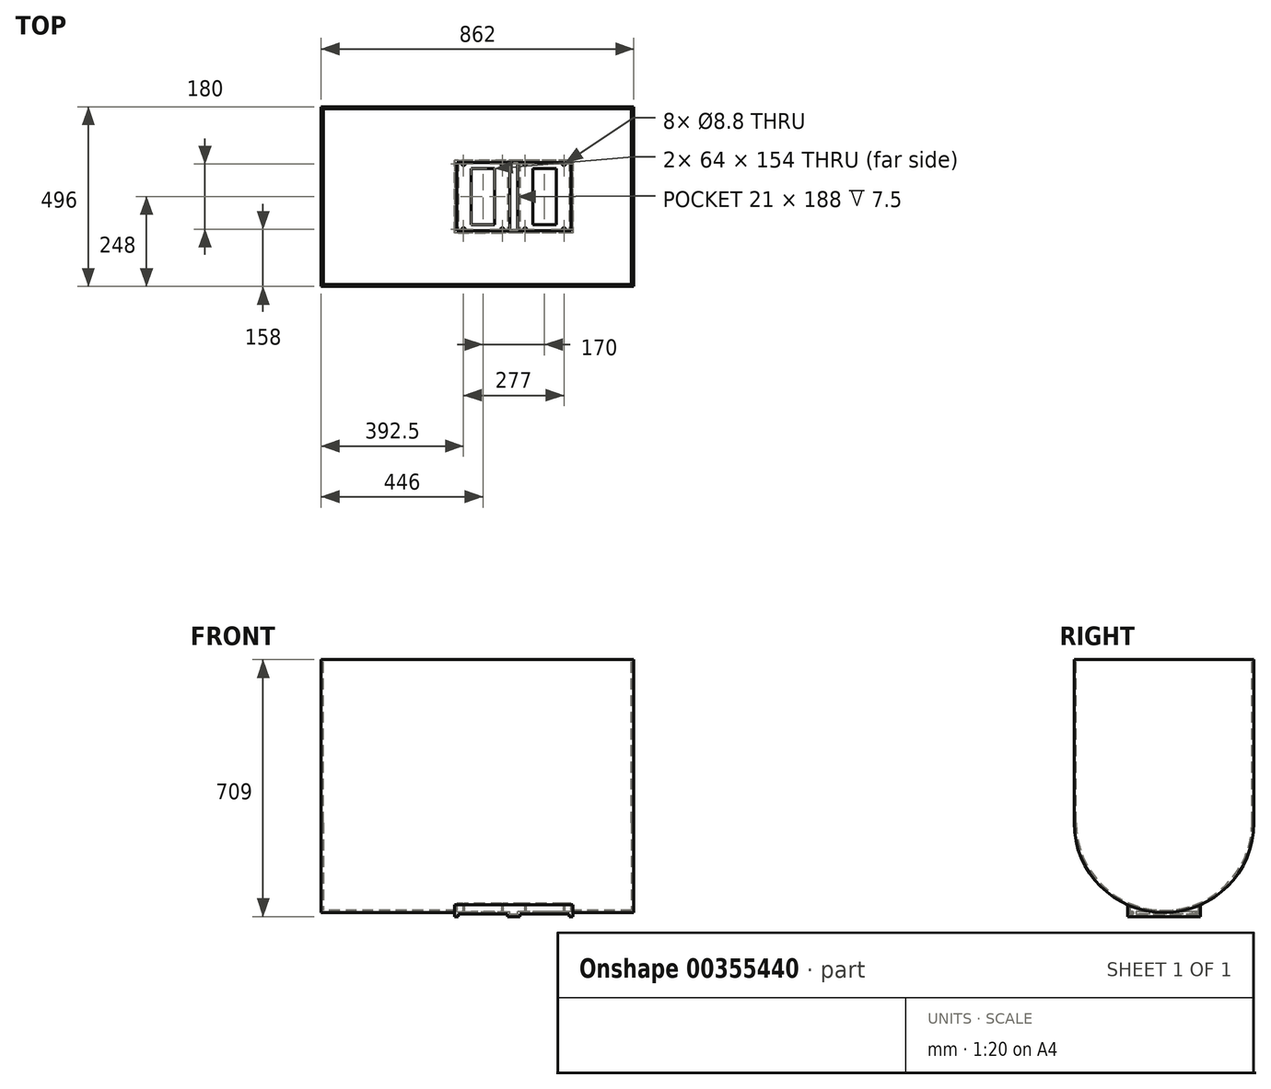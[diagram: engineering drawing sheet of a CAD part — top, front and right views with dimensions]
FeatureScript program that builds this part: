
annotation { "Feature Type Name" : "Feature", "Feature Type Description" : "" }
export const myFeature = defineFeature(function(context is Context, id is Id, definition is map)
    precondition{}
    {
        {
            var Q0;
            Q0=qCreatedBy(makeId("Right.planeOp"),FACE);
            var sketch = newSketch(context, id + "F0", { "sketchPlane" : qUnion([Q0])});
            skArc(sketch, "E0", {"start": v(-248, 0) * mm, "mid": v(0, -248) * mm, "end": v(248, 0) * mm});
            skLineSegment(sketch, "E1", {"start": v(0, -259) * mm, "end": v(0, 710.2) * mm, "construction": true});
            skLineSegment(sketch, "E2.0", {"start": v(248, 0) * mm, "end": v(248, 450) * mm});
            skLineSegment(sketch, "E3.MirrorCS", {"start": v(-248, 0) * mm, "end": v(-248, 450) * mm});
            skLineSegment(sketch, "E4", {"start": v(-248, 0) * mm, "end": v(248, 0) * mm, "construction": true});
            skLineSegment(sketch, "E5.MirrorCS", {"start": v(-248, 450) * mm, "end": v(248, 450) * mm});
            skPoint(sketch, "E6.orphan", {"position": v(-248, 710.2) * mm});
            skPoint(sketch, "E7.orphan", {"position": v(248, 710.2) * mm});
            skLineSegment(sketch, "E8.bottom", {"start": v(100, -259) * mm, "end": v(-100, -259) * mm});
            skLineSegment(sketch, "E8.left", {"start": v(100, -259) * mm, "end": v(100, -226.94) * mm});
            skLineSegment(sketch, "E8.right", {"start": v(-100, -259) * mm, "end": v(-100, -226.94) * mm});
            skPoint(sketch, "E8.middle", {"position": v(0, -248) * mm});
            skPoint(sketch, "E9.orphan", {"position": v(-100, -237) * mm});
            skPoint(sketch, "E10.orphan", {"position": v(100, -237) * mm});
            skSolve(sketch);
        }
        {
            var Q0;
            {var subQ0=sQuery(id+"F0.wireOp",EDGE,"E2.0");Q0=makeQuery(id+"F0.imprint","IMPRINT",FACE,{"disambiguationData":[TD([[makeQuery(id+"F0.imprint","IMPRINT",EDGE,{"derivedFrom":subQ0}),1.0]])]});}
            extrude(context, id + "F1", {"entities" : qUnion([Q0]), "endBound" : BoundingType.SYMMETRIC, "depth" : 862 * mm});
        }
        {
            var Q0;
            Q0=makeQuery(id+"F0.imprint","IMPRINT",FACE,{"disambiguationData":[TD([[makeQuery(id+"F0.imprint","IMPRINT",EDGE,{"derivedFrom":sQuery(id+"F0.wireOp",EDGE,"E8.bottom")}),-1.0]])]});
            extrude(context, id + "F2", {"entities" : qUnion([Q0]), "operationType" : NewBodyOperationType.ADD, "depth" : 263.5 * mm, "hasSecondDirection" : true, "secondDirectionOppositeDirection" : true, "secondDirectionDepth" : 63.5 * mm});
        }
        {
            var Q0;
            Q0=makeQuery(id+"F2.opExtrude","SWEPT_FACE",FACE,{"disambiguationData":[OSD([sQuery(id+"F0.wireOp",EDGE,"E8.right")])]});
            var sketch = newSketch(context, id + "F3", { "sketchPlane" : qUnion([Q0])});
            skLineSegment(sketch, "E11.bottom", {"start": v(-53.5, -269) * mm, "end": v(83.5, -269) * mm});
            skLineSegment(sketch, "E11.top", {"start": v(-53.5, -251.5) * mm, "end": v(83.5, -251.5) * mm});
            skLineSegment(sketch, "E11.left", {"start": v(-53.5, -269) * mm, "end": v(-53.5, -251.5) * mm});
            skLineSegment(sketch, "E11.right", {"start": v(83.5, -269) * mm, "end": v(83.5, -251.5) * mm});
            skLineSegment(sketch, "E12", {"start": v(100, -259) * mm, "end": v(100, -189.41) * mm, "construction": true});
            skLineSegment(sketch, "E13.MirrorCS", {"start": v(253.5, -269) * mm, "end": v(116.5, -269) * mm});
            skLineSegment(sketch, "E14.MirrorCS", {"start": v(253.5, -251.5) * mm, "end": v(116.5, -251.5) * mm});
            skLineSegment(sketch, "E15.MirrorCS", {"start": v(116.5, -269) * mm, "end": v(116.5, -251.5) * mm});
            skLineSegment(sketch, "E16.MirrorCS", {"start": v(253.5, -269) * mm, "end": v(253.5, -251.5) * mm});
            skSolve(sketch);
        }
        {
            var Q0;
            Q0 = qSketchRegion(id + "F3", true);
            extrude(context, id + "F4", {"entities" : qUnion([Q0]), "operationType" : NewBodyOperationType.REMOVE, "oppositeDirection" : true, "depth" : 250 * mm});
        }
        {
            var Q0;
            Q0=makeQuery(id+"F1.opExtrude","SWEPT_FACE",FACE,{"disambiguationData":[OSD([sQuery(id+"F0.wireOp",EDGE,"E5.MirrorCS")])]});
            shell(context, id + "F5", {"entities" : qUnion([Q0]), "thickness" : 6 * mm});
        }
        {
            var Q0;
            Q0=makeQuery(id+"F4.boolean.opBoolean","COPY",FACE,{"derivedFrom":makeQuery(id+"F4.opExtrude","SWEPT_FACE",FACE,{"disambiguationData":[OSD([sQuery(id+"F3.wireOp",EDGE,"E14.MirrorCS")])]})});
            var sketch = newSketch(context, id + "F6", { "sketchPlane" : qUnion([Q0])});
            skLineSegment(sketch, "E17.bottom", {"start": v(153, 77) * mm, "end": v(217, 77) * mm});
            skLineSegment(sketch, "E17.top", {"start": v(153, -77) * mm, "end": v(217, -77) * mm});
            skLineSegment(sketch, "E17.left", {"start": v(153, 77) * mm, "end": v(153, -77) * mm});
            skLineSegment(sketch, "E17.right", {"start": v(217, 77) * mm, "end": v(217, -77) * mm});
            skLineSegment(sketch, "E18", {"start": v(100, 100) * mm, "end": v(100, -121.49) * mm, "construction": true});
            skLineSegment(sketch, "E19.MirrorCS", {"start": v(-17, 77) * mm, "end": v(-17, -77) * mm});
            skLineSegment(sketch, "E20.MirrorCS", {"start": v(47, 77) * mm, "end": v(47, -77) * mm});
            skLineSegment(sketch, "E21.MirrorCS", {"start": v(47, -77) * mm, "end": v(-17, -77) * mm});
            skLineSegment(sketch, "E22.MirrorCS", {"start": v(47, 77) * mm, "end": v(-17, 77) * mm});
            skSolve(sketch);
        }
        {
            var Q0;
            Q0=makeQuery(id+"F6.imprint","IMPRINT",FACE,{"disambiguationData":[TD([[makeQuery(id+"F6.imprint","IMPRINT",EDGE,{"derivedFrom":sQuery(id+"F6.wireOp",EDGE,"E19.MirrorCS")}),1.0]])]});
            var Q1;
            Q1=makeQuery(id+"F6.imprint","IMPRINT",FACE,{"disambiguationData":[TD([[makeQuery(id+"F6.imprint","IMPRINT",EDGE,{"derivedFrom":sQuery(id+"F6.wireOp",EDGE,"E17.bottom")}),-1.0]])]});
            extrude(context, id + "F7", {"entities" : qUnion([Q0, Q1]), "operationType" : NewBodyOperationType.REMOVE, "oppositeDirection" : true, "depth" : 50 * mm});
        }
        {
            var Q0;
            Q0=makeQuery(id+"F4.boolean.opBoolean","COPY",FACE,{"derivedFrom":makeQuery(id+"F4.opExtrude","SWEPT_FACE",FACE,{"disambiguationData":[OSD([sQuery(id+"F3.wireOp",EDGE,"E11.top")])]})});
            var sketch = newSketch(context, id + "F8", { "sketchPlane" : qUnion([Q0])});
            skLineSegment(sketch, "E23.bottom", {"start": v(-38.5, 90) * mm, "end": v(68.5, 90) * mm, "construction": true});
            skLineSegment(sketch, "E23.top", {"start": v(-38.5, -90) * mm, "end": v(68.5, -90) * mm, "construction": true});
            skLineSegment(sketch, "E23.left", {"start": v(-38.5, 90) * mm, "end": v(-38.5, -90) * mm, "construction": true});
            skLineSegment(sketch, "E23.right", {"start": v(68.5, 90) * mm, "end": v(68.5, -90) * mm, "construction": true});
            skPoint(sketch, "E24.0", {"position": v(100, 100) * mm});
            skLineSegment(sketch, "E25", {"start": v(100, 100) * mm, "end": v(100, 159.34) * mm, "construction": true});
            skLineSegment(sketch, "E26.MirrorCS", {"start": v(238.5, 90) * mm, "end": v(131.5, 90) * mm, "construction": true});
            skLineSegment(sketch, "E27.MirrorCS", {"start": v(131.5, 90) * mm, "end": v(131.5, -90) * mm, "construction": true});
            skLineSegment(sketch, "E28.MirrorCS", {"start": v(238.5, 90) * mm, "end": v(238.5, -90) * mm, "construction": true});
            skLineSegment(sketch, "E29.MirrorCS", {"start": v(238.5, -90) * mm, "end": v(131.5, -90) * mm, "construction": true});
            skSolve(sketch);
        }
        {
            var Q0;
            Q0=sQuery(id+"F8.wireOp",VERTEX,"E23.bottom.start");
            var Q1;
            Q1=sQuery(id+"F8.wireOp",VERTEX,"E23.bottom.end");
            var Q2;
            Q2=sQuery(id+"F8.wireOp",VERTEX,"E23.right.end");
            var Q3;
            Q3=sQuery(id+"F8.wireOp",VERTEX,"E23.top.start");
            var Q4;
            Q4=makeQuery(id+"F1.opExtrude","SWEPT_BODY",BODY,{"disambiguationData":[OSD([sQuery(id+"F0.wireOp",EDGE,"E0"),sQuery(id+"F0.wireOp",EDGE,"E2.0"),sQuery(id+"F0.wireOp",EDGE,"E3.MirrorCS"),sQuery(id+"F0.wireOp",EDGE,"E5.MirrorCS")])]});
            hole(context, id + "F9", {"style" : HoleStyle.SIMPLE, "endStyle" : HoleEndStyle.THROUGH, "standardTappedOrClearance" : lookupTablePath({ "standard" : "ISO", "fit" : "Normal", "size" : "M8", "type" : "Clearance" }), "standardBlindInLast" : lookupTablePath({ "fit" : "Standard", "standard" : "ISO", "size" : "M8", "type" : "Clearance" }), "holeDiameter" : 8.8 * mm, "isTappedThrough" : true, "tappedDepth" : 12 * mm, "tapClearance" : 3, "startFromSketch" : true, "locations" : qUnion([Q0, Q1, Q2, Q3]), "scope" : qUnion([Q4])});
        }
        {
            var Q0;
            Q0=sQuery(id+"F8.wireOp",VERTEX,"E27.MirrorCS.start");
            var Q1;
            Q1=sQuery(id+"F8.wireOp",VERTEX,"E28.MirrorCS.start");
            var Q2;
            Q2=sQuery(id+"F8.wireOp",VERTEX,"E28.MirrorCS.end");
            var Q3;
            Q3=sQuery(id+"F8.wireOp",VERTEX,"E27.MirrorCS.end");
            var Q4;
            Q4=makeQuery(id+"F1.opExtrude","SWEPT_BODY",BODY,{"disambiguationData":[OSD([sQuery(id+"F0.wireOp",EDGE,"E0"),sQuery(id+"F0.wireOp",EDGE,"E2.0"),sQuery(id+"F0.wireOp",EDGE,"E3.MirrorCS"),sQuery(id+"F0.wireOp",EDGE,"E5.MirrorCS")])]});
            hole(context, id + "F10", {"style" : HoleStyle.SIMPLE, "endStyle" : HoleEndStyle.THROUGH, "standardTappedOrClearance" : lookupTablePath({ "standard" : "ISO", "fit" : "Normal", "size" : "M8", "type" : "Clearance" }), "standardBlindInLast" : lookupTablePath({ "fit" : "Standard", "standard" : "ISO", "size" : "M8", "type" : "Clearance" }), "holeDiameter" : 8.8 * mm, "isTappedThrough" : true, "tappedDepth" : 12 * mm, "tapClearance" : 3, "startFromSketch" : true, "locations" : qUnion([Q0, Q1, Q2, Q3]), "scope" : qUnion([Q4])});
        }
    });
